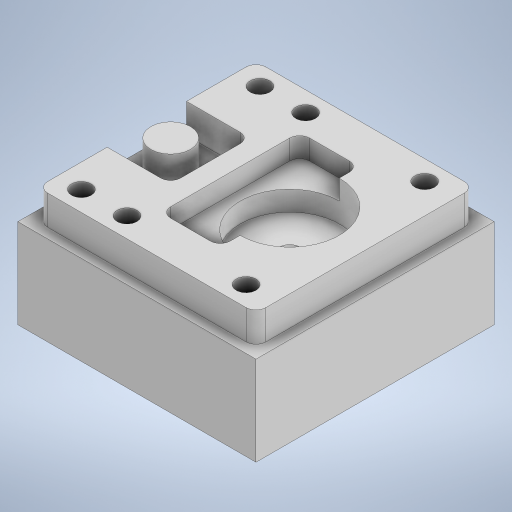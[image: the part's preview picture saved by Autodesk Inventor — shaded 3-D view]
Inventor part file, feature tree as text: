
AUTODESK INVENTOR PART (.ipt)
format: ipt  version: 2023.2 (Build 272271000, 271)  size: 321,536 bytes
history: native  units: mm
features: extrude x7, sketch x7
ambient origin geometry x8: Origin, YZ Plane, XZ Plane, XY Plane, X Axis, Y Axis, Z Axis, Center Point
bodies: Solid1 (feature_tree)
feature tree (14):
  extrude  "Extrusion1"  Depth=60.0mm
  extrude  "Extrusion2"  Depth=55.0mm
  extrude  "Extrusion3"  Depth=2.5mm
  extrude  "Extrusion4"  Depth=25.0mm
  extrude  "Extrusion5"  Depth=10.0mm TaperAngle=0.0deg
  extrude  "Extrusion6"  Depth=35.0mm
  extrude  "Extrusion7"  Depth=2.5mm
  sketch  "Sketch1"  dims[d0=60.0mm d1=60.0mm]
  sketch  "Sketch2"  dims[d2=22.5mm d3=0.0mm d4=55.0mm]
  sketch  "Sketch3"  dims[d5=55.0mm d6=2.5mm]
  sketch  "Sketch4"  dims[d7=7.5mm d8=0.0mm d9=25.0mm]
  sketch  "Sketch5"  dims[d10=21.5mm d11=10.0mm d12=0.0mm]
  sketch  "Sketch6"  dims[d13=15.0mm d14=35.0mm]
  sketch  "Sketch7"  dims[d15=36.5mm d16=2.5mm d17=5.0mm d18=0.0mm d19=16.0mm d20=20.0mm d21=41.5mm d22=2.5mm d23=10.0mm d24=51.5mm d25=7.5mm d26=0.0mm d27=5.0mm d28=12.5mm d29=0.0mm d30=5.0mm d31=10.0mm d32=7.5mm d33=20.0mm d35=45.0mm d36=10.0mm d38=10.0mm d40=5.0mm d41=40.0mm d42=20.0mm d44=45.0mm d45=20.0mm d47=11.5mm d50=10.0mm d51=0.0mm]
